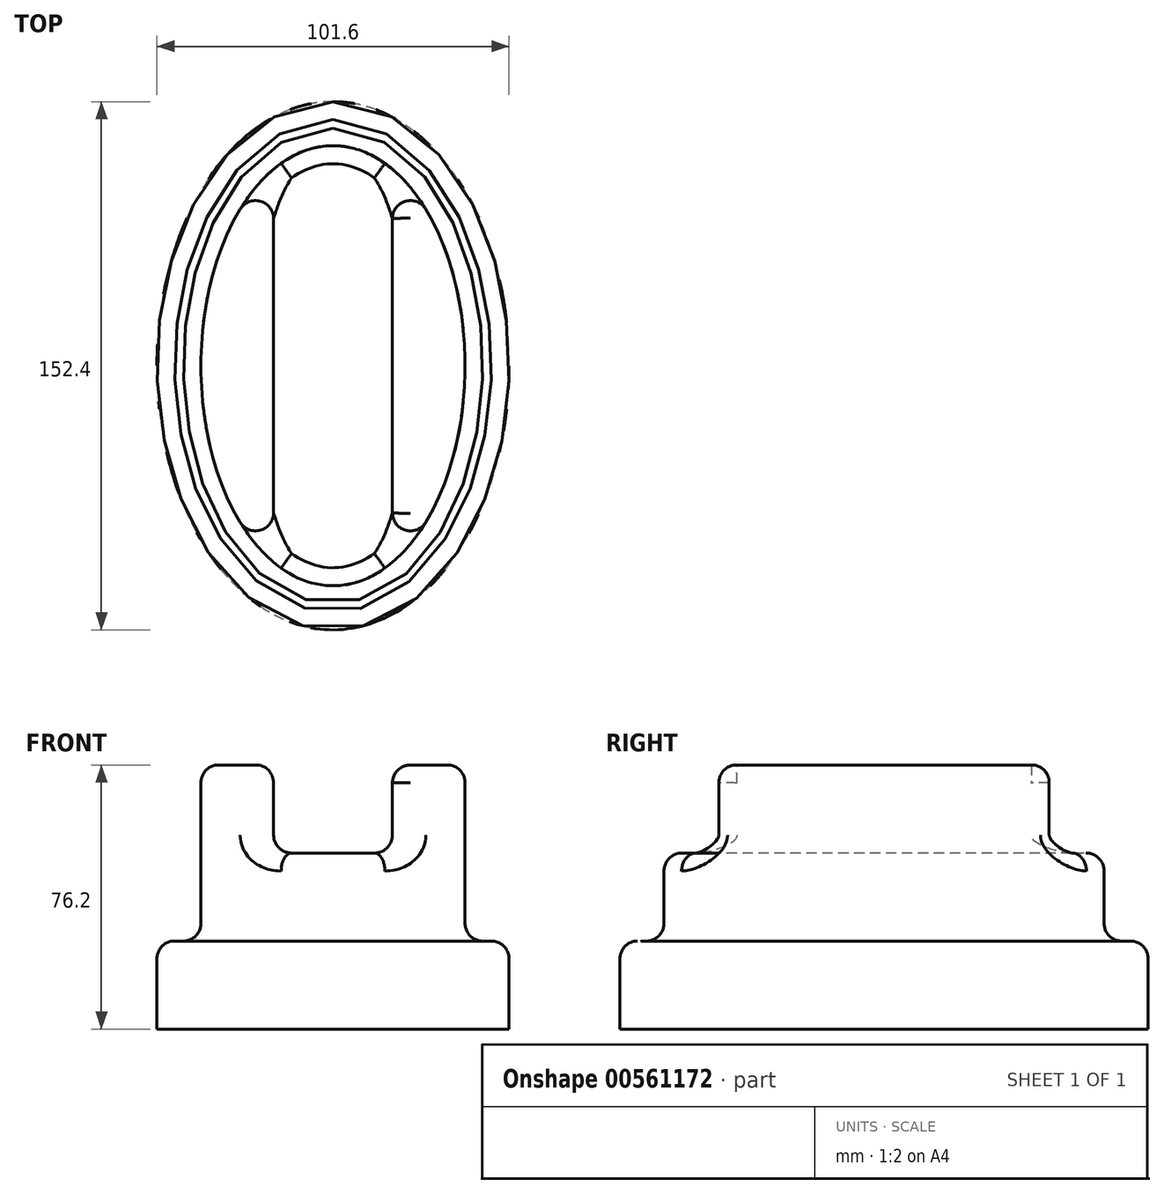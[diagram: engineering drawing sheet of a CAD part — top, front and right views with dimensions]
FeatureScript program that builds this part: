
annotation { "Feature Type Name" : "Feature", "Feature Type Description" : "" }
export const myFeature = defineFeature(function(context is Context, id is Id, definition is map)
    precondition{}
    {
        {
            var Q0;
            Q0=qCreatedBy(makeId("Top.planeOp"),FACE);
            var sketch = newSketch(context, id + "F0", { "sketchPlane" : qUnion([Q0])});
            skEllipse(sketch, "E0", {"center": v(0, 0) * mm, "majorRadius": 76.2 * mm, "minorRadius": 50.8 * mm, "majorAxis": v(0, 1)});
            skSolve(sketch);
        }
        {
            var Q0;
            Q0 = qSketchRegion(id + "F0", true);
            extrude(context, id + "F1", {"entities" : qUnion([Q0]), "depth" : 25.4 * mm, "offsetDistance" : 25.4 * mm});
        }
        {
            var Q0;
            Q0=makeQuery(id+"F1.opExtrude","CAP_FACE",FACE,{"disambiguationData":[OSD([sQuery(id+"F0.wireOp",EDGE,"E0")])],"isStart":false});
            var sketch = newSketch(context, id + "F2", { "sketchPlane" : qUnion([Q0])});
            skEllipse(sketch, "E1", {"center": v(0, 0) * mm, "majorRadius": 63.5 * mm, "minorRadius": 38.1 * mm, "majorAxis": v(0, 1)});
            skSolve(sketch);
        }
        {
            var Q0;
            Q0 = qSketchRegion(id + "F2", true);
            extrude(context, id + "F3", {"entities" : qUnion([Q0]), "operationType" : NewBodyOperationType.ADD, "depth" : 50.8 * mm, "offsetDistance" : 25.4 * mm});
        }
        {
            var Q0;
            Q0=makeQuery(id+"F3.opExtrude","CAP_FACE",FACE,{"disambiguationData":[OSD([sQuery(id+"F2.wireOp",EDGE,"E1")])],"isStart":false});
            var sketch = newSketch(context, id + "F4", { "sketchPlane" : qUnion([Q0])});
            skLineSegment(sketch, "E2.bottom", {"start": v(-17.15, 63.5) * mm, "end": v(17.15, 63.5) * mm});
            skLineSegment(sketch, "E2.top", {"start": v(-17.15, -63.5) * mm, "end": v(17.15, -63.5) * mm});
            skLineSegment(sketch, "E2.left", {"start": v(-17.15, 63.5) * mm, "end": v(-17.15, -63.5) * mm});
            skLineSegment(sketch, "E2.right", {"start": v(17.15, 63.5) * mm, "end": v(17.15, -63.5) * mm});
            skPoint(sketch, "E2.middle", {"position": v(0, 0) * mm});
            skPoint(sketch, "E2.cornerSnap0", {"position": v(0, 63.5) * mm});
            skSolve(sketch);
        }
        {
            var Q0;
            Q0 = qSketchRegion(id + "F4", true);
            extrude(context, id + "F5", {"entities" : qUnion([Q0]), "operationType" : NewBodyOperationType.REMOVE, "oppositeDirection" : true, "depth" : 25.4 * mm, "offsetDistance" : 25.4 * mm});
        }
        {
            var Q0;
            Q0=makeQuery(id+"F5.boolean.opBoolean","COPY",EDGE,{"derivedFrom":makeQuery(id+"F5.opExtrude","CAP_EDGE",EDGE,{"disambiguationData":[OSD([sQuery(id+"F4.wireOp",EDGE,"E2.left")])],"isStart":true})});
            var Q1;
            Q1=makeQuery(id+"F5.boolean.opBoolean","COPY",EDGE,{"derivedFrom":makeQuery(id+"F5.opExtrude","CAP_EDGE",EDGE,{"disambiguationData":[OSD([sQuery(id+"F4.wireOp",EDGE,"E2.left")])],"isStart":false})});
            var Q2;
            Q2=makeQuery(id+"F5.boolean.opBoolean","INTERSECT",EDGE,{"disambiguationData":[OD(0.0)],"derivedFrom":[makeQuery(id+"F3.opExtrude","SWEPT_FACE",FACE,{"disambiguationData":[OSD([sQuery(id+"F2.wireOp",EDGE,"E1")])]}),makeQuery(id+"F5.opExtrude","CAP_FACE",FACE,{"disambiguationData":[OSD([sQuery(id+"F4.wireOp",EDGE,"E2.bottom"),sQuery(id+"F4.wireOp",EDGE,"E2.top"),sQuery(id+"F4.wireOp",EDGE,"E2.left"),sQuery(id+"F4.wireOp",EDGE,"E2.right")])],"isStart":false})]});
            var Q3;
            Q3=makeQuery(id+"F5.boolean.opBoolean","COPY",EDGE,{"derivedFrom":makeQuery(id+"F5.opExtrude","CAP_EDGE",EDGE,{"disambiguationData":[OSD([sQuery(id+"F4.wireOp",EDGE,"E2.right")])],"isStart":false})});
            var Q4;
            Q4=makeQuery(id+"F5.boolean.opBoolean","COPY",FACE,{"derivedFrom":makeQuery(id+"F5.opExtrude","SWEPT_FACE",FACE,{"disambiguationData":[OSD([sQuery(id+"F4.wireOp",EDGE,"E2.right")])]})});
            var Q5;
            Q5=makeQuery(id+"F5.boolean.opBoolean","INTERSECT",EDGE,{"disambiguationData":[OD(0.0)],"derivedFrom":[makeQuery(id+"F3.opExtrude","SWEPT_FACE",FACE,{"disambiguationData":[OSD([sQuery(id+"F2.wireOp",EDGE,"E1")])]}),makeQuery(id+"F5.opExtrude","SWEPT_FACE",FACE,{"disambiguationData":[OSD([sQuery(id+"F4.wireOp",EDGE,"E2.left")])]})]});
            var Q6;
            Q6=makeQuery(id+"F5.boolean.opBoolean","INTERSECT",EDGE,{"disambiguationData":[OD(1.0)],"derivedFrom":[makeQuery(id+"F3.opExtrude","SWEPT_FACE",FACE,{"disambiguationData":[OSD([sQuery(id+"F2.wireOp",EDGE,"E1")])]}),makeQuery(id+"F5.opExtrude","CAP_FACE",FACE,{"disambiguationData":[OSD([sQuery(id+"F4.wireOp",EDGE,"E2.bottom"),sQuery(id+"F4.wireOp",EDGE,"E2.top"),sQuery(id+"F4.wireOp",EDGE,"E2.left"),sQuery(id+"F4.wireOp",EDGE,"E2.right")])],"isStart":false})]});
            var Q7;
            Q7=makeQuery(id+"F5.boolean.opBoolean","INTERSECT",EDGE,{"disambiguationData":[OD(1.0)],"derivedFrom":[makeQuery(id+"F3.opExtrude","SWEPT_FACE",FACE,{"disambiguationData":[OSD([sQuery(id+"F2.wireOp",EDGE,"E1")])]}),makeQuery(id+"F5.opExtrude","SWEPT_FACE",FACE,{"disambiguationData":[OSD([sQuery(id+"F4.wireOp",EDGE,"E2.left")])]})]});
            fillet(context, id + "F6", {"entities" : qUnion([Q0, Q1, Q2, Q3, Q4, Q5, Q6, Q7]), "radius" : 5.2 * mm, "tangentPropagation" : true, "allowEdgeOverflow" : false});
        }
        {
            var Q0;
            Q0=makeQuery(id+"F1.opExtrude","CAP_FACE",FACE,{"disambiguationData":[OSD([sQuery(id+"F0.wireOp",EDGE,"E0")])],"isStart":false});
            fillet(context, id + "F7", {"entities" : qUnion([Q0]), "radius" : 5.08 * mm, "tangentPropagation" : true, "allowEdgeOverflow" : false});
        }
        {
            var Q0;
            {var subQ0=sQuery(id+"F2.wireOp",EDGE,"E1");Q0=makeQuery(id+"F5.boolean.opBoolean","SPLIT",FACE,{"disambiguationData":[TD([makeQuery(id+"F5.opExtrude","SWEPT_FACE",FACE,{"disambiguationData":[OSD([sQuery(id+"F4.wireOp",EDGE,"E2.left")])]})])],"derivedFrom":makeQuery(id+"F3.opExtrude","CAP_FACE",FACE,{"disambiguationData":[OSD([subQ0])],"isStart":false})});}
            var Q1;
            {var subQ0=sQuery(id+"F2.wireOp",EDGE,"E1");Q1=makeQuery(id+"F5.boolean.opBoolean","SPLIT",FACE,{"disambiguationData":[TD([makeQuery(id+"F5.opExtrude","SWEPT_FACE",FACE,{"disambiguationData":[OSD([sQuery(id+"F4.wireOp",EDGE,"E2.right")])]})])],"derivedFrom":makeQuery(id+"F3.opExtrude","CAP_FACE",FACE,{"disambiguationData":[OSD([subQ0])],"isStart":false})});}
            fillet(context, id + "F8", {"entities" : qUnion([Q0, Q1]), "radius" : 5.08 * mm, "tangentPropagation" : true, "allowEdgeOverflow" : false});
        }
    });
